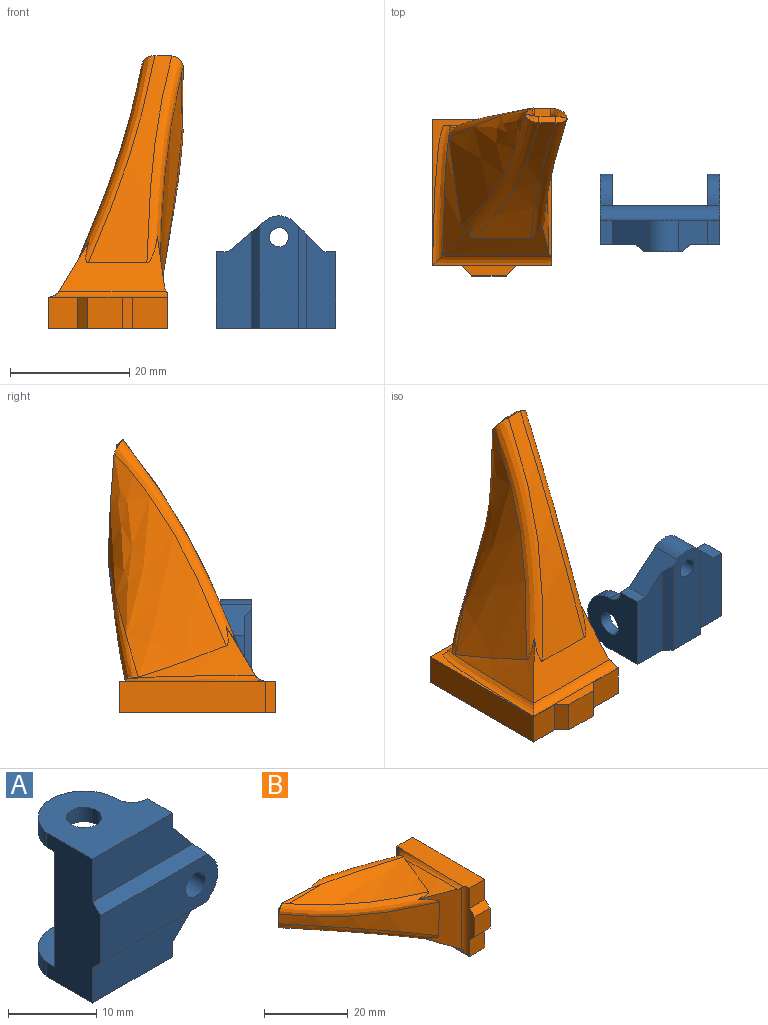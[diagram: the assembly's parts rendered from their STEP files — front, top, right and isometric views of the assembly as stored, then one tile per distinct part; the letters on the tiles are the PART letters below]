
ASSEMBLY  parts=2 mates=1
PART A: 27 faces, bbox 18.8x13x20 mm
  f0: plane 20x1.52mm, normal (-0.71,0.71,0), area 34.5mm2, adj f2,f7,f10,f11,f19,f20,f24,f25
  f1: plane 16x2.32mm, normal (0.72,0.69,0), area 51.7mm2, adj f2,f9,f20,f25
  f2: cylinder r=4mm len=16mm, axis (0,0,1), area 126mm2, adj f0,f1,f20,f25
  f3: plane 16x6mm, normal (0,1,0), area 47.9mm2, adj f7,f13,f15,f16,f18
  f4: plane 18.82x6.56mm, normal (0,-1,0), area 111.7mm2, adj f6,f9,f12,f13,f15,f16,f18
  f5: plane 15.74x4.92mm, normal (0,-1,0), area 67.4mm2, adj f6,f9,f10,f17,f18
  f6: plane 17.04x1.3mm, normal (0,-0.71,-0.71), area 30.1mm2, adj f4,f5,f9,f18
  f7: cylinder r=2.5mm len=20mm, axis (0,0,1), area 77.5mm2, adj f0,f3,f10,f11,f14,f17
  f8: plane 16.09x5.92mm, normal (0,-1,0), area 82.4mm2, adj f9,f11,f12,f14,f16
  f9: plane 20x8.71mm, normal (-1,0,0), area 136.5mm2, adj f1,f4,f5,f6,f8,f10,f11,f12
  f10: plane 12.82x11.7mm, normal (0,0,-1), area 108.3mm2, adj f0,f5,f7,f9,f17,f19,f21,f22
  f11: plane 12.82x11.7mm, normal (0,0,1), area 108.3mm2, adj f0,f7,f8,f9,f14,f23,f24,f26
  f12: plane 17.17x1.3mm, normal (0,-0.71,0.71), area 30.5mm2, adj f4,f8,f9,f16
  f13: cylinder r=1.6mm len=5.3mm, axis (0,1,0), area 53.3mm2, adj f3,f4
  f14: plane 4x2mm, normal (1,0,0), area 8mm2, adj f7,f8,f11,f16
  f15: cylinder r=3.6mm len=5.3mm, axis (0,1,0), area 28.2mm2, adj f3,f4,f16,f18
  f16: plane 6.19x5.3mm, normal (0.77,0,0.64), area 35mm2, adj f3,f4,f8,f12,f14,f15
  f17: plane 4x2mm, normal (1,0,0), area 8mm2, adj f5,f7,f10,f18
  f18: plane 5.3x4.96mm, normal (0.71,0,-0.71), area 30.6mm2, adj f3,f4,f5,f6,f15,f17
  f19: plane 2x0.05mm, normal (1,0,0), area 0.1mm2, adj f0,f10,f20,f22
  f20: plane 10.32x9.2mm, normal (0,0,1), area 57.4mm2, adj f0,f1,f2,f9,f19,f21,f22
  f21: cylinder r=2mm len=4mm, axis (0,0,-1), area 25.1mm2, adj f10,f20
  f22: cylinder r=5.2mm len=10.32mm, axis (0,0,-1), area 30.8mm2, adj f9,f10,f19,f20
  f23: cylinder r=5.2mm len=10.32mm, axis (0,0,-1), area 30.8mm2, adj f9,f11,f24,f25
  f24: plane 2x0.05mm, normal (1,0,0), area 0.1mm2, adj f0,f11,f23,f25
  f25: plane 10.32x9.2mm, normal (0,0,-1), area 57.4mm2, adj f0,f1,f2,f9,f23,f24,f26
  f26: cylinder r=2mm len=4mm, axis (0,0,-1), area 25.1mm2, adj f11,f25
PART B: 53 faces, bbox 51.3x34.7x39.1 mm
  f0: bspline ~24.5x16.68mm, area 43.6mm2, adj f21,f35,f41,f52
  f1: plane 3.08x0.89mm, normal (-0.45,0.9,0), area 1mm2, adj f20,f22,f37,f50
  f2: plane 23.2x17.2mm, normal (1,0,0), area 111.5mm2, adj f3,f4,f5,f6,f7,f8,f9,f18
  f3: plane 3.2x3mm, normal (0,1,0), area 9.6mm2, adj f2,f4,f18,f19
  f4: plane 3.2x1.5mm, normal (0,0,1), area 4.8mm2, adj f2,f3,f5,f19
  f5: plane 7x3.2mm, normal (0,1,0), area 22.4mm2, adj f2,f4,f6,f19
  f6: plane 21.5x3.2mm, normal (0,0,1), area 68.8mm2, adj f2,f5,f7,f19
  f7: plane 17x3.2mm, normal (0,-1,0), area 54.4mm2, adj f2,f6,f8,f19
  f8: plane 21.5x3.2mm, normal (0,0,-1), area 68.8mm2, adj f2,f7,f9,f19
  f9: plane 7x3.2mm, normal (0,1,0), area 22.4mm2, adj f2,f8,f18,f19
  f10: plane 5.77x5.2mm, normal (0,-1,0), area 30mm2, adj f11,f17,f19,f20
  f11: plane 5.2x1.69mm, normal (0,-0.71,0.71), area 12.4mm2, adj f10,f12,f19,f20
  f12: plane 5.92x5.2mm, normal (0,-1,0), area 30.8mm2, adj f11,f13,f19,f20
  f13: plane 24.53x5.87mm, normal (0,0,1), area 135.6mm2, adj f12,f14,f19,f20,f51,f52
  f14: plane 20x5.2mm, normal (0,1,0), area 104mm2, adj f13,f15,f19,f20
  f15: plane 24.5x5.2mm, normal (0,0,-1), area 127.4mm2, adj f14,f16,f19,f20
  f16: plane 5.2x4.92mm, normal (0,-1,0), area 25.6mm2, adj f15,f17,f19,f20
  f17: plane 5.2x1.69mm, normal (0,-0.71,-0.71), area 12.4mm2, adj f10,f16,f19,f20
  f18: plane 3.2x1.5mm, normal (0,0,-1), area 4.8mm2, adj f2,f3,f9,f19
  f19: plane 26.19x20mm, normal (1,0,0), area 132.6mm2, adj f3,f4,f5,f6,f7,f8,f9,f10
  f20: plane 26.19x20mm, normal (-1,0,0), area 45.6mm2, adj f1,f10,f11,f12,f13,f14,f15,f16
  f21: bspline ~20.5x16.69mm, area 95.9mm2, adj f0,f22,f35,f39,f40,f50,f51,f52
  f22: bspline ~24.5x16.64mm, area 67.4mm2, adj f1,f21,f37,f38,f39,f50
  f23: plane 3.19x0.91mm, normal (-0.45,0.9,0), area 1mm2, adj f20,f24,f34,f52
  f24: bspline ~24.5x16.68mm, area 0mm2, adj f23,f34,f52
  f25: bspline ~22.39x18.25mm, area 177.5mm2, adj f2,f31,f32,f46
  f26: bspline ~41.55x22mm, area 395.9mm2, adj f2,f30,f31,f44
  f27: bspline ~41.55x22mm, area 276.6mm2, adj f2,f29,f30,f42
  f28: bspline ~41.55x22mm, area 495.5mm2, adj f2,f29,f32,f48
  f29: bspline ~46.52x25.38mm, area 50mm2, adj f2,f27,f28,f49
  f30: bspline ~47.62x25.39mm, area 49.7mm2, adj f2,f26,f27,f43
  f31: bspline ~32.81x5.64mm, area 36.1mm2, adj f2,f25,f26,f45
  f32: bspline ~25.29x15.53mm, area 19.4mm2, adj f2,f25,f28,f47
  f33: offset ~21.93x3.78mm, area 7.6mm2, adj f34,f35,f41,f44
  f34: bspline ~30.9x7.62mm, area 94.6mm2, adj f20,f23,f24,f33,f36,f41,f45,f52
  f35: bspline ~41.33x23.19mm, area 114mm2, adj f0,f21,f33,f40,f41,f43
  f36: offset ~22.85x19.29mm, area 150.2mm2, adj f20,f34,f37,f46
  f37: bspline ~23.26x15.7mm, area 49.3mm2, adj f1,f20,f22,f36,f38,f47
  f38: offset ~44.35x24.8mm, area 442.8mm2, adj f22,f37,f39,f48
  f39: bspline ~38.07x23.7mm, area 119.3mm2, adj f21,f22,f38,f40,f49
  f40: offset ~37.17x21.95mm, area 191.4mm2, adj f21,f35,f39,f42
  f41: offset ~40.12x20.42mm, area 317.5mm2, adj f0,f33,f34,f35,f52
  f42: bspline ~2.83x1.11mm, area 4mm2, adj f27,f40,f43,f49
  f43: bspline ~1.9x1.73mm, area 2.8mm2, adj f30,f35,f42,f44
  f44: bspline ~9.22x1.34mm, area 12.9mm2, adj f26,f33,f43,f45
  f45: bspline ~9.24x2.81mm, area 13.7mm2, adj f31,f34,f44,f46
  f46: bspline ~2.73x1.39mm, area 3.8mm2, adj f25,f36,f45,f47
  f47: bspline ~1.39x0.34mm, area 0.4mm2, adj f32,f37,f46,f48
  f48: bspline ~17.62x1.38mm, area 24.7mm2, adj f28,f38,f47,f49
  f49: bspline ~2.28x2.27mm, area 4mm2, adj f29,f39,f42,f48
  f50: bspline ~28.26x3.22mm, area 42mm2, adj f1,f20,f21,f22,f51
  f51: bspline ~35.89x1.74mm, area 39.5mm2, adj f13,f20,f21,f50,f52
  f52: bspline ~25.12x3.19mm, area 32.1mm2, adj f0,f13,f20,f21,f23,f24,f34,f41
PLACE A rot(axis=(0,-1,0),90deg) t=(51.35,4.14,-77.25)mm fixed
PLACE B rot(axis=(0,1,0),90deg) t=(2.2,0.51,35.63)mm
MATE planar B.f19 <-> A.f9  axis (0,0,-1) through (19.74,10.51,-0.77)mm
